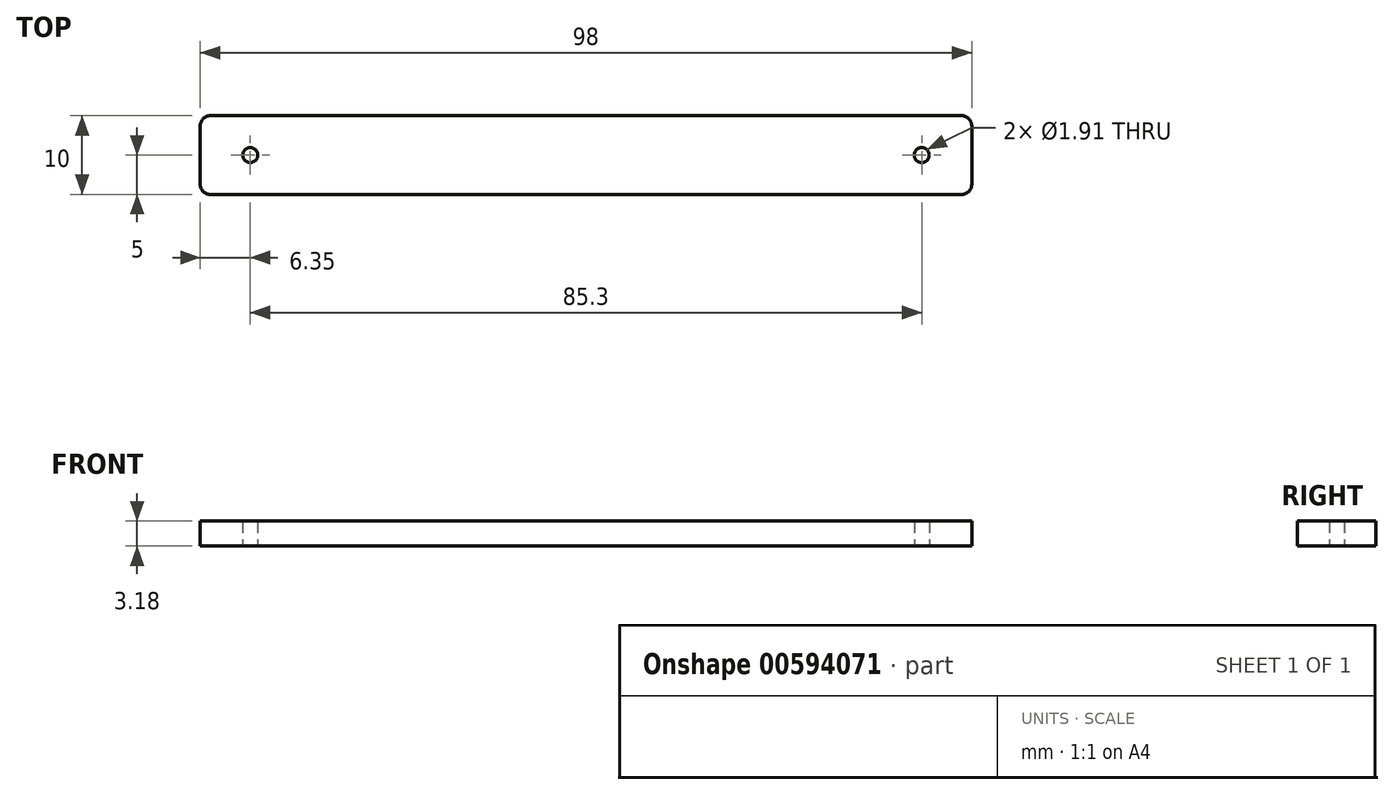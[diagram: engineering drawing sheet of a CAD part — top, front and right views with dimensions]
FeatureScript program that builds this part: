
annotation { "Feature Type Name" : "Feature", "Feature Type Description" : "" }
export const myFeature = defineFeature(function(context is Context, id is Id, definition is map)
    precondition{}
    {
        {
            var Q0;
            Q0=qCreatedBy(makeId("Top.planeOp"),FACE);
            var sketch = newSketch(context, id + "F0", { "sketchPlane" : qUnion([Q0])});
            skLineSegment(sketch, "E0.bottom", {"start": v(1.27, 0) * mm, "end": v(96.73, 0) * mm});
            skLineSegment(sketch, "E0.top", {"start": v(1.27, -10) * mm, "end": v(96.73, -10) * mm});
            skLineSegment(sketch, "E0.left", {"start": v(0, -1.27) * mm, "end": v(0, -8.73) * mm});
            skLineSegment(sketch, "E0.right", {"start": v(98, -1.27) * mm, "end": v(98, -8.73) * mm});
            skPoint(sketch, "E1.visualSharp", {"position": v(0, 0) * mm});
            skArc(sketch, "E1.filletArc", {"start": v(1.27, 0) * mm, "mid": v(0.37, -0.37) * mm, "end": v(0, -1.27) * mm});
            skPoint(sketch, "E2.visualSharp", {"position": v(0, -10) * mm});
            skArc(sketch, "E2.filletArc", {"start": v(0, -8.73) * mm, "mid": v(0.37, -9.63) * mm, "end": v(1.27, -10) * mm});
            skPoint(sketch, "E3.visualSharp", {"position": v(98, -10) * mm});
            skArc(sketch, "E3.filletArc", {"start": v(96.73, -10) * mm, "mid": v(97.63, -9.63) * mm, "end": v(98, -8.73) * mm});
            skPoint(sketch, "E4.visualSharp", {"position": v(98, 0) * mm});
            skArc(sketch, "E4.filletArc", {"start": v(98, -1.27) * mm, "mid": v(97.63, -0.37) * mm, "end": v(96.73, 0) * mm});
            skCircle(sketch, "E5", {"center": v(6.35, -5) * mm, "radius": 0.95 * mm});
            skLineSegment(sketch, "E6", {"start": v(0, -5) * mm, "end": v(6.35, -5) * mm, "construction": true});
            skCircle(sketch, "E7", {"center": v(91.65, -5) * mm, "radius": 0.95 * mm});
            skLineSegment(sketch, "E8", {"start": v(91.65, -5) * mm, "end": v(98, -5) * mm, "construction": true});
            skSolve(sketch);
        }
        {
            var Q0;
            Q0=makeQuery(id+"F0.imprint","IMPRINT",FACE,{"disambiguationData":[TD([[makeQuery(id+"F0.imprint","IMPRINT",EDGE,{"derivedFrom":sQuery(id+"F0.wireOp",EDGE,"E0.bottom")}),-1.0]])]});
            extrude(context, id + "F1", {"entities" : qUnion([Q0]), "depth" : 3.17 * mm, "offsetDistance" : 25.4 * mm});
        }
    });
